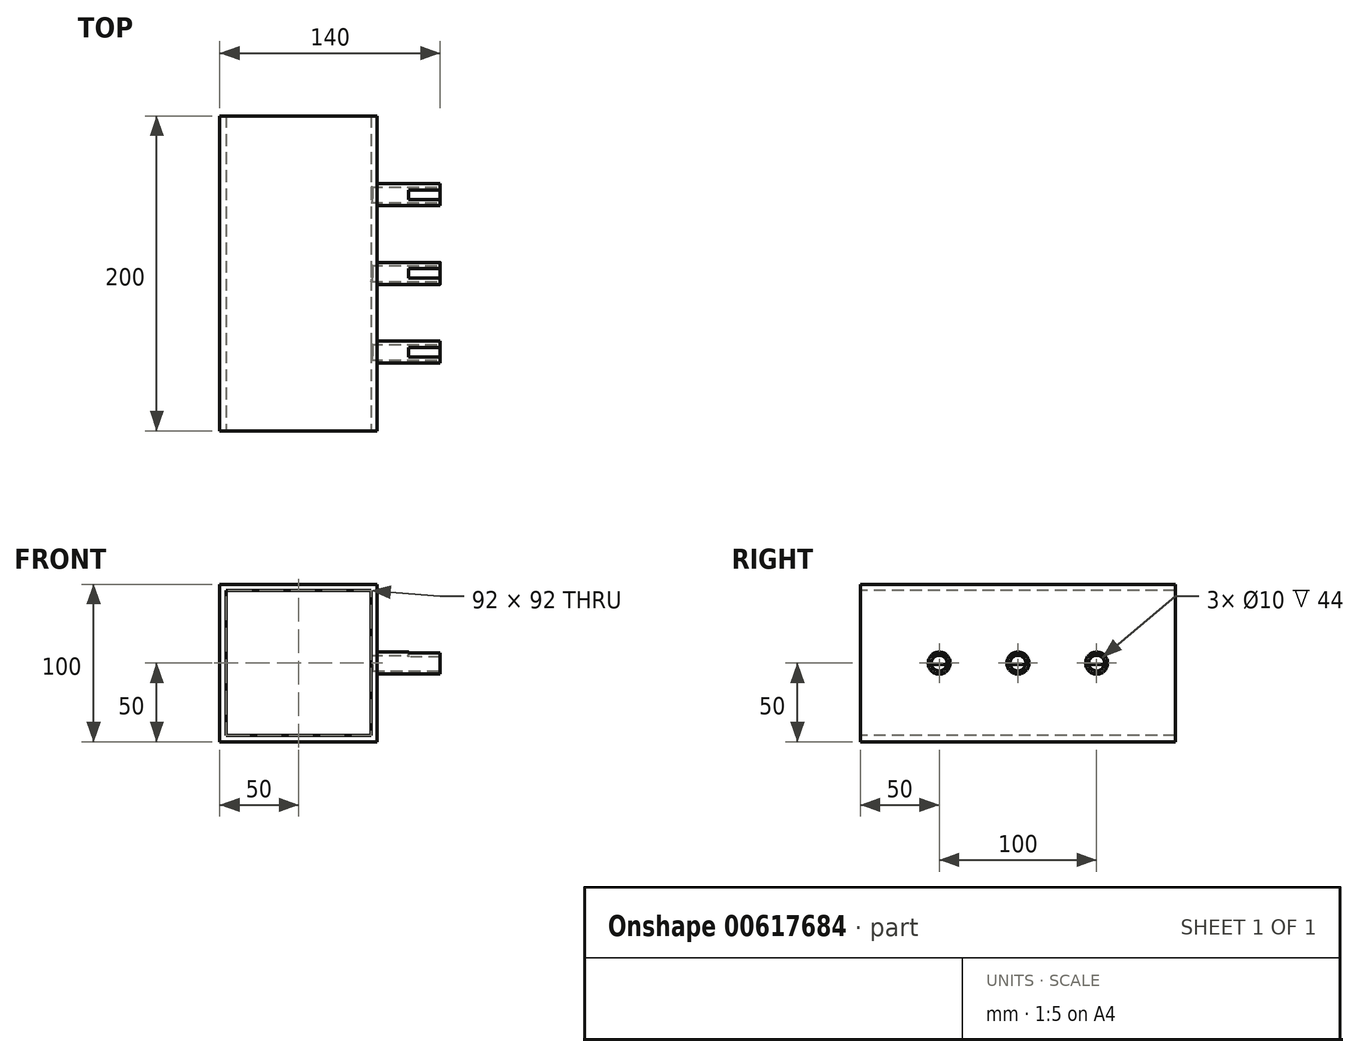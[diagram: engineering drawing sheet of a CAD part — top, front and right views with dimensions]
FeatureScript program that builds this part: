
annotation { "Feature Type Name" : "Feature", "Feature Type Description" : "" }
export const myFeature = defineFeature(function(context is Context, id is Id, definition is map)
    precondition{}
    {
        {
            var Q0;
            Q0=qCreatedBy(makeId("Front.planeOp"),FACE);
            var sketch = newSketch(context, id + "F0", { "sketchPlane" : qUnion([Q0])});
            skLineSegment(sketch, "E0.bottom", {"start": v(0, 0) * mm, "end": v(100, 0) * mm});
            skLineSegment(sketch, "E0.top", {"start": v(0, 100) * mm, "end": v(100, 100) * mm});
            skLineSegment(sketch, "E0.left", {"start": v(0, 0) * mm, "end": v(0, 100) * mm});
            skLineSegment(sketch, "E0.right", {"start": v(100, 0) * mm, "end": v(100, 100) * mm});
            skSolve(sketch);
        }
        {
            var Q0;
            Q0 = qSketchRegion(id + "F0", true);
            extrude(context, id + "F1", {"entities" : qUnion([Q0]), "oppositeDirection" : true, "depth" : 200 * mm, "offsetDistance" : 25.4 * mm});
        }
        {
            var Q0;
            Q0=makeQuery(id+"F1.opExtrude","CAP_FACE",FACE,{"disambiguationData":[OSD([sQuery(id+"F0.wireOp",EDGE,"E0.bottom"),sQuery(id+"F0.wireOp",EDGE,"E0.top"),sQuery(id+"F0.wireOp",EDGE,"E0.left"),sQuery(id+"F0.wireOp",EDGE,"E0.right")])],"isStart":true});
            var sketch = newSketch(context, id + "F2", { "sketchPlane" : qUnion([Q0])});
            skLineSegment(sketch, "E1", {"start": v(0, 0) * mm, "end": v(0, 4) * mm});
            skLineSegment(sketch, "E2", {"start": v(0, 4) * mm, "end": v(4, 4) * mm});
            skLineSegment(sketch, "E3.bottom", {"start": v(4, 4) * mm, "end": v(96, 4) * mm});
            skLineSegment(sketch, "E3.top", {"start": v(4, 96) * mm, "end": v(96, 96) * mm});
            skLineSegment(sketch, "E3.left", {"start": v(4, 4) * mm, "end": v(4, 96) * mm});
            skLineSegment(sketch, "E3.right", {"start": v(96, 4) * mm, "end": v(96, 96) * mm});
            skSolve(sketch);
        }
        {
            var Q0;
            Q0=makeQuery(id+"F2.imprint","IMPRINT",FACE,{"disambiguationData":[TD([[makeQuery(id+"F2.imprint","IMPRINT",EDGE,{"derivedFrom":sQuery(id+"F2.wireOp",EDGE,"E3.bottom")}),1.0]])]});
            extrude(context, id + "F3", {"entities" : qUnion([Q0]), "operationType" : NewBodyOperationType.REMOVE, "oppositeDirection" : true, "depth" : 200 * mm, "offsetDistance" : 25.4 * mm});
        }
        {
            var Q0;
            Q0=makeQuery(id+"F1.opExtrude","SWEPT_FACE",FACE,{"disambiguationData":[OSD([sQuery(id+"F0.wireOp",EDGE,"E0.right")])]});
            var sketch = newSketch(context, id + "F4", { "sketchPlane" : qUnion([Q0])});
            skCircle(sketch, "E4", {"center": v(50, 50) * mm, "radius": 5 * mm});
            skCircle(sketch, "E5", {"center": v(100, 50) * mm, "radius": 5 * mm});
            skCircle(sketch, "E6", {"center": v(150, 50) * mm, "radius": 5 * mm});
            skCircle(sketch, "E7", {"center": v(50, 50) * mm, "radius": 7 * mm});
            skCircle(sketch, "E8", {"center": v(100, 50) * mm, "radius": 7 * mm});
            skCircle(sketch, "E9", {"center": v(150, 50) * mm, "radius": 7 * mm});
            skSolve(sketch);
        }
        {
            var Q0;
            Q0=makeQuery(id+"F4.imprint","IMPRINT",FACE,{"disambiguationData":[TD([[makeQuery(id+"F4.imprint","IMPRINT",EDGE,{"derivedFrom":sQuery(id+"F4.wireOp",EDGE,"E4")}),1.0]])]});
            var Q1;
            Q1=makeQuery(id+"F4.imprint","IMPRINT",FACE,{"disambiguationData":[TD([[makeQuery(id+"F4.imprint","IMPRINT",EDGE,{"derivedFrom":sQuery(id+"F4.wireOp",EDGE,"E5")}),1.0]])]});
            var Q2;
            Q2=makeQuery(id+"F4.imprint","IMPRINT",FACE,{"disambiguationData":[TD([[makeQuery(id+"F4.imprint","IMPRINT",EDGE,{"derivedFrom":sQuery(id+"F4.wireOp",EDGE,"E6")}),1.0]])]});
            extrude(context, id + "F5", {"entities" : qUnion([Q0, Q1, Q2]), "operationType" : NewBodyOperationType.REMOVE, "oppositeDirection" : true, "depth" : 4 * mm, "offsetDistance" : 25.4 * mm});
        }
        {
            var Q0;
            Q0=makeQuery(id+"F4.imprint","IMPRINT",FACE,{"disambiguationData":[TD([[makeQuery(id+"F4.imprint","IMPRINT",EDGE,{"derivedFrom":sQuery(id+"F4.wireOp",EDGE,"E4")}),-1.0]])]});
            var Q1;
            Q1=makeQuery(id+"F4.imprint","IMPRINT",FACE,{"disambiguationData":[TD([[makeQuery(id+"F4.imprint","IMPRINT",EDGE,{"derivedFrom":sQuery(id+"F4.wireOp",EDGE,"E5")}),-1.0]])]});
            var Q2;
            Q2=makeQuery(id+"F4.imprint","IMPRINT",FACE,{"disambiguationData":[TD([[makeQuery(id+"F4.imprint","IMPRINT",EDGE,{"derivedFrom":sQuery(id+"F4.wireOp",EDGE,"E6")}),-1.0]])]});
            extrude(context, id + "F6", {"entities" : qUnion([Q0, Q1, Q2]), "operationType" : NewBodyOperationType.ADD, "depth" : 20 * mm, "offsetDistance" : 25.4 * mm});
        }
        {
            var Q0;
            Q0=makeQuery(id+"F6.opExtrude","CAP_FACE",FACE,{"disambiguationData":[OSD([sQuery(id+"F4.wireOp",EDGE,"E4"),sQuery(id+"F4.wireOp",EDGE,"E7")])],"isStart":false});
            var sketch = newSketch(context, id + "F7", { "sketchPlane" : qUnion([Q0])});
            skArc(sketch, "E10", {"start": v(47, 56.33) * mm, "mid": v(50, 43) * mm, "end": v(53, 56.33) * mm});
            skLineSegment(sketch, "E11", {"start": v(53, 56.33) * mm, "end": v(53, 56.33) * mm});
            skArc(sketch, "E12", {"start": v(47, 54) * mm, "mid": v(50, 45) * mm, "end": v(53, 54) * mm});
            skLineSegment(sketch, "E13", {"start": v(47, 54) * mm, "end": v(47, 56.33) * mm});
            skLineSegment(sketch, "E14", {"start": v(53, 54) * mm, "end": v(53, 56.32) * mm});
            skLineSegment(sketch, "E15.1.0.0", {"start": v(103, 54) * mm, "end": v(103, 56.32) * mm});
            skArc(sketch, "E15.1.0.1", {"start": v(97, 56.33) * mm, "mid": v(100, 43) * mm, "end": v(103, 56.33) * mm});
            skArc(sketch, "E15.1.0.2", {"start": v(97, 54) * mm, "mid": v(100, 45) * mm, "end": v(103, 54) * mm});
            skLineSegment(sketch, "E15.1.0.3", {"start": v(97, 54) * mm, "end": v(97, 56.33) * mm});
            skLineSegment(sketch, "E15.2.0.0", {"start": v(153, 54) * mm, "end": v(153, 56.32) * mm});
            skArc(sketch, "E15.2.0.1", {"start": v(147, 56.33) * mm, "mid": v(150, 43) * mm, "end": v(153, 56.33) * mm});
            skArc(sketch, "E15.2.0.2", {"start": v(147, 54) * mm, "mid": v(150, 45) * mm, "end": v(153, 54) * mm});
            skLineSegment(sketch, "E15.2.0.3", {"start": v(147, 54) * mm, "end": v(147, 56.33) * mm});
            skLineSegment(sketch, "E15.direction1", {"start": v(50, 50) * mm, "end": v(100, 50) * mm, "construction": true});
            skSolve(sketch);
        }
        {
            var Q0;
            Q0=makeQuery(id+"F3.boolean.opBoolean","COPY",FACE,{"derivedFrom":makeQuery(id+"F3.opExtrude","SWEPT_FACE",FACE,{"disambiguationData":[OSD([sQuery(id+"F2.wireOp",EDGE,"E3.right")])]})});
            var sketch = newSketch(context, id + "F8", { "sketchPlane" : qUnion([Q0])});
            skLineSegment(sketch, "E16", {"start": v(-50, 49.17) * mm, "end": v(-54.93, 49.17) * mm});
            skLineSegment(sketch, "E17", {"start": v(-50, 49.17) * mm, "end": v(-45.07, 49.17) * mm});
            skArc(sketch, "E18", {"start": v(-54.93, 49.17) * mm, "mid": v(-50, 45) * mm, "end": v(-45.07, 49.17) * mm});
            skLineSegment(sketch, "E19.1.0.0", {"start": v(-100, 49.17) * mm, "end": v(-95.07, 49.17) * mm});
            skLineSegment(sketch, "E19.1.0.1", {"start": v(-100, 49.17) * mm, "end": v(-104.93, 49.17) * mm});
            skArc(sketch, "E19.1.0.2", {"start": v(-104.93, 49.17) * mm, "mid": v(-100, 45) * mm, "end": v(-95.07, 49.17) * mm});
            skLineSegment(sketch, "E19.2.0.0", {"start": v(-150, 49.17) * mm, "end": v(-145.07, 49.17) * mm});
            skLineSegment(sketch, "E19.2.0.1", {"start": v(-150, 49.17) * mm, "end": v(-154.93, 49.17) * mm});
            skArc(sketch, "E19.2.0.2", {"start": v(-154.93, 49.17) * mm, "mid": v(-150, 45) * mm, "end": v(-145.07, 49.17) * mm});
            skLineSegment(sketch, "E19.direction1", {"start": v(-54.93, 49.17) * mm, "end": v(-104.93, 49.17) * mm, "construction": true});
            skLineSegment(sketch, "E20", {"start": v(-54.93, 49.17) * mm, "end": v(-45.07, 49.17) * mm});
            skSolve(sketch);
        }
        {
            var Q0;
            Q0 = qSketchRegion(id + "F8", true);
            extrude(context, id + "F9", {"entities" : qUnion([Q0]), "operationType" : NewBodyOperationType.ADD, "oppositeDirection" : true, "depth" : 1 * mm, "offsetDistance" : 25.4 * mm});
        }
        {
            var Q0;
            Q0=makeQuery(id+"F7.imprint","IMPRINT",FACE,{"disambiguationData":[TD([[makeQuery(id+"F7.imprint","IMPRINT",EDGE,{"derivedFrom":sQuery(id+"F7.wireOp",EDGE,"E12")}),-1.0]])]});
            var Q1;
            {var subQ0=sQuery(id+"F7.wireOp",EDGE,"E15.1.0.0");Q1=makeQuery(id+"F7.imprint","IMPRINT",FACE,{"disambiguationData":[TD([[makeQuery(id+"F7.imprint","IMPRINT",EDGE,{"derivedFrom":subQ0}),-1.0]])]});}
            var Q2;
            {var subQ0=sQuery(id+"F7.wireOp",EDGE,"E15.2.0.0");Q2=makeQuery(id+"F7.imprint","IMPRINT",FACE,{"disambiguationData":[TD([[makeQuery(id+"F7.imprint","IMPRINT",EDGE,{"derivedFrom":subQ0}),-1.0]])]});}
            extrude(context, id + "F10", {"entities" : qUnion([Q0, Q1, Q2]), "operationType" : NewBodyOperationType.ADD, "depth" : 20 * mm, "offsetDistance" : 25.4 * mm});
        }
    });
